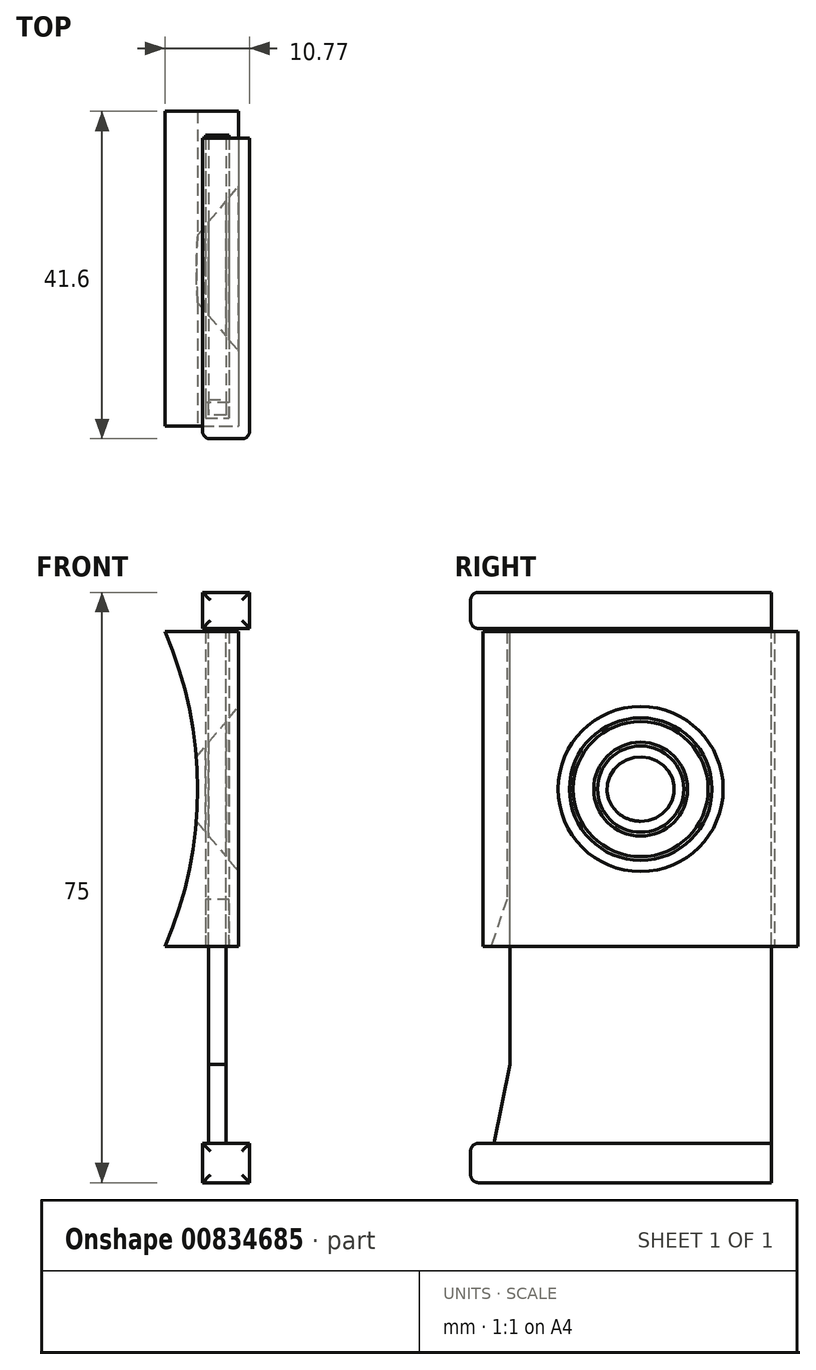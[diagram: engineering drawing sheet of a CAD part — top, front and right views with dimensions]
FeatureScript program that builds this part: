
annotation { "Feature Type Name" : "Feature", "Feature Type Description" : "" }
export const myFeature = defineFeature(function(context is Context, id is Id, definition is map)
    precondition{}
    {
        {
            var Q0;
            Q0=qCreatedBy(makeId("Top.planeOp"),FACE);
            var sketch = newSketch(context, id + "F0", { "sketchPlane" : qUnion([Q0])});
            skLineSegment(sketch, "E0.bottom", {"start": v(0, 20) * mm, "end": v(10, 20) * mm});
            skLineSegment(sketch, "E0.top", {"start": v(0, -20) * mm, "end": v(10, -20) * mm});
            skLineSegment(sketch, "E0.left", {"start": v(0, 20) * mm, "end": v(0, -20) * mm});
            skLineSegment(sketch, "E0.right", {"start": v(10, 20) * mm, "end": v(10, -20) * mm});
            skCircle(sketch, "E1", {"center": v(-41.2, 0) * mm, "radius": 50 * mm});
            skLineSegment(sketch, "E2.bottom", {"start": v(10, 20) * mm, "end": v(13, 20) * mm});
            skLineSegment(sketch, "E2.top", {"start": v(10, 17) * mm, "end": v(13, 17) * mm});
            skLineSegment(sketch, "E2.left", {"start": v(10, 20) * mm, "end": v(10, 17) * mm});
            skLineSegment(sketch, "E2.right", {"start": v(13, 20) * mm, "end": v(13, 17) * mm});
            skLineSegment(sketch, "E3.bottom", {"start": v(10, -20) * mm, "end": v(13, -20) * mm});
            skLineSegment(sketch, "E3.top", {"start": v(10, -17) * mm, "end": v(13, -17) * mm});
            skLineSegment(sketch, "E3.left", {"start": v(10, -20) * mm, "end": v(10, -17) * mm});
            skLineSegment(sketch, "E3.right", {"start": v(13, -20) * mm, "end": v(13, -17) * mm});
            skLineSegment(sketch, "E4.bottom", {"start": v(13, 20) * mm, "end": v(14.2, 20) * mm});
            skLineSegment(sketch, "E4.top", {"start": v(13, -20) * mm, "end": v(14.2, -20) * mm});
            skLineSegment(sketch, "E4.left", {"start": v(13, 20) * mm, "end": v(13, -20) * mm});
            skLineSegment(sketch, "E4.right", {"start": v(14.2, 20) * mm, "end": v(14.2, -20) * mm});
            skLineSegment(sketch, "E5.left", {"start": v(13, -20) * mm, "end": v(13, -20) * mm});
            skLineSegment(sketch, "E5.right", {"start": v(14.2, -20) * mm, "end": v(14.2, -20) * mm});
            skSolve(sketch);
        }
        {
            var Q0;
            Q0=makeQuery(id+"F0.imprint","IMPRINT",FACE,{"disambiguationData":[TD([[makeQuery(id+"F0.imprint","IMPRINT",EDGE,{"derivedFrom":sQuery(id+"F0.wireOp",EDGE,"E0.right")}),-1.0]])]});
            var Q1;
            {var subQ0=sQuery(id+"F0.wireOp",EDGE,"E2.bottom");Q1=makeQuery(id+"F0.imprint","IMPRINT",FACE,{"disambiguationData":[TD([[makeQuery(id+"F0.imprint","IMPRINT",EDGE,{"derivedFrom":subQ0}),-1.0]])]});}
            var Q2;
            {var subQ4=sQuery(id+"F0.wireOp",EDGE,"E4.bottom");Q2=makeQuery(id+"F0.imprint","IMPRINT",FACE,{"disambiguationData":[TD([[makeQuery(id+"F0.imprint","IMPRINT",EDGE,{"derivedFrom":subQ4}),-1.0]])]});}
            var Q3;
            {var subQ0=sQuery(id+"F0.wireOp",EDGE,"E3.bottom");Q3=makeQuery(id+"F0.imprint","IMPRINT",FACE,{"disambiguationData":[TD([[makeQuery(id+"F0.imprint","IMPRINT",EDGE,{"derivedFrom":subQ0}),1.0]])]});}
            var Q4;
            {var subQ0=sQuery(id+"F0.wireOp",EDGE,"E0.left");Q4=makeQuery(id+"F0.imprint","IMPRINT",FACE,{"disambiguationData":[TD([[makeQuery(id+"F0.imprint","IMPRINT",EDGE,{"derivedFrom":subQ0}),1.0]])]});}
            extrude(context, id + "F1", {"entities" : qUnion([Q0, Q1, Q2, Q3, Q4]), "endBound" : BoundingType.SYMMETRIC, "depth" : 40 * mm, "offsetDistance" : 25 * mm});
        }
        {
            var Q0;
            Q0=qCreatedBy(makeId("Front.planeOp"),FACE);
            var sketch = newSketch(context, id + "F2", { "sketchPlane" : qUnion([Q0])});
            skCircle(sketch, "E6", {"center": v(-41, 0) * mm, "radius": 50 * mm});
            skSolve(sketch);
        }
        {
            var Q0;
            Q0=qSketchRegion(id+"F2",true);
            extrude(context, id + "F3", {"entities" : qUnion([Q0]), "operationType" : NewBodyOperationType.REMOVE, "endBound" : BoundingType.SYMMETRIC, "oppositeDirection" : true, "depth" : 50 * mm, "offsetDistance" : 25 * mm});
        }
        {
            var Q0;
            Q0=makeQuery(id+"F1.opExtrude","CAP_FACE",FACE,{"disambiguationData":[OSD([sQuery(id+"F0.wireOp",EDGE,"E0.bottom"),sQuery(id+"F0.wireOp",EDGE,"E0.top"),sQuery(id+"F0.wireOp",EDGE,"E0.left"),sQuery(id+"F0.wireOp",EDGE,"E0.right"),sQuery(id+"F0.wireOp",EDGE,"E2.bottom"),sQuery(id+"F0.wireOp",EDGE,"E2.top"),sQuery(id+"F0.wireOp",EDGE,"E3.bottom"),sQuery(id+"F0.wireOp",EDGE,"E3.top"),sQuery(id+"F0.wireOp",EDGE,"E4.bottom"),sQuery(id+"F0.wireOp",EDGE,"E4.left"),sQuery(id+"F0.wireOp",EDGE,"E4.right"),sQuery(id+"F0.wireOp",EDGE,"E4.top")])],"isStart":false});
            var sketch = newSketch(context, id + "F4", { "sketchPlane" : qUnion([Q0])});
            skLineSegment(sketch, "E7.bottom", {"start": v(10.4, 16.6) * mm, "end": v(12.6, 16.6) * mm});
            skLineSegment(sketch, "E7.top", {"start": v(10.4, -16.6) * mm, "end": v(12.6, -16.6) * mm});
            skLineSegment(sketch, "E7.left", {"start": v(10.4, 16.6) * mm, "end": v(10.4, -16.6) * mm});
            skLineSegment(sketch, "E7.right", {"start": v(12.6, 16.6) * mm, "end": v(12.6, -16.6) * mm});
            skSolve(sketch);
        }
        {
            var Q0;
            Q0=makeQuery(id+"F4.imprint","IMPRINT",FACE,{"disambiguationData":[TD([[makeQuery(id+"F4.imprint","IMPRINT",EDGE,{"derivedFrom":sQuery(id+"F4.wireOp",EDGE,"E7.bottom")}),-1.0]])]});
            extrude(context, id + "F5", {"entities" : qUnion([Q0]), "oppositeDirection" : true, "depth" : 70 * mm, "offsetDistance" : 25 * mm, "hasSecondDirection" : true, "secondDirectionOppositeDirection" : false, "secondDirectionDepth" : 5 * mm});
        }
        {
            var Q0;
            Q0=qCreatedBy(makeId("Right.planeOp"),FACE);
            cPlane(context, id + "F6", {"entities" : qUnion([Q0]), "cplaneType" : CPlaneType.OFFSET, "offset" : 7.92 * mm, "width" : 150 * mm, "height" : 150 * mm});
        }
        {
            var Q0;
            Q0=qCreatedBy(id+"F6.planeOp",FACE);
            var sketch = newSketch(context, id + "F7", { "sketchPlane" : qUnion([Q0])});
            skCircle(sketch, "E8", {"center": v(0, 0) * mm, "radius": 3 * mm});
            skSolve(sketch);
        }
        {
            var Q0;
            Q0=qSketchRegion(id+"F7",true);
            extrude(context, id + "F8", {"entities" : qUnion([Q0]), "operationType" : NewBodyOperationType.REMOVE, "depth" : 25 * mm, "offsetDistance" : 25 * mm, "hasDraft" : true, "draftAngle" : 50 * degree});
        }
        {
            var Q0;
            Q0=makeQuery(id+"F5.opExtrude","SWEPT_FACE",FACE,{"disambiguationData":[OSD([sQuery(id+"F4.wireOp",EDGE,"E7.right")])]});
            var sketch = newSketch(context, id + "F9", { "sketchPlane" : qUnion([Q0])});
            skLineSegment(sketch, "E9.bottom", {"start": v(16.6, 25) * mm, "end": v(-21.6, 25) * mm});
            skLineSegment(sketch, "E9.top", {"start": v(16.6, 20.4) * mm, "end": v(-21.6, 20.4) * mm});
            skLineSegment(sketch, "E9.left", {"start": v(16.6, 25) * mm, "end": v(16.6, 20.4) * mm});
            skLineSegment(sketch, "E9.right", {"start": v(-21.6, 25) * mm, "end": v(-21.6, 20.4) * mm});
            skLineSegment(sketch, "E10.bottom", {"start": v(16.6, -50) * mm, "end": v(-21.6, -50) * mm});
            skLineSegment(sketch, "E10.top", {"start": v(16.6, -45) * mm, "end": v(-21.6, -45) * mm});
            skLineSegment(sketch, "E10.left", {"start": v(16.6, -50) * mm, "end": v(16.6, -45) * mm});
            skLineSegment(sketch, "E10.right", {"start": v(-21.6, -50) * mm, "end": v(-21.6, -45) * mm});
            skSolve(sketch);
        }
        {
            var Q0;
            Q0=qSketchRegion(id+"F9",true);
            extrude(context, id + "F10", {"entities" : qUnion([Q0]), "operationType" : NewBodyOperationType.ADD, "depth" : 3 * mm, "offsetDistance" : 25 * mm, "hasSecondDirection" : true, "secondDirectionOppositeDirection" : true, "secondDirectionDepth" : 3 * mm});
        }
        {
            var Q0;
            Q0=makeQuery(id+"F10.opExtrude","SWEPT_FACE",FACE,{"disambiguationData":[OSD([sQuery(id+"F9.wireOp",EDGE,"E10.right")])]});
            var Q1;
            Q1=makeQuery(id+"F10.opExtrude","SWEPT_FACE",FACE,{"disambiguationData":[OSD([sQuery(id+"F9.wireOp",EDGE,"E9.right")])]});
            fillet(context, id + "F11", {"entities" : qUnion([Q0, Q1]), "radius" : 1 * mm, "tangentPropagation" : true, "allowEdgeOverflow" : false});
        }
        {
            var Q0;
            Q0=makeQuery(id+"F10.boolean.opBoolean","INTERSECT",EDGE,{"derivedFrom":[makeQuery(id+"F5.opExtrude","SWEPT_FACE",FACE,{"disambiguationData":[OSD([sQuery(id+"F4.wireOp",EDGE,"E7.top")])]}),makeQuery(id+"F10.opExtrude","SWEPT_FACE",FACE,{"disambiguationData":[OSD([sQuery(id+"F9.wireOp",EDGE,"E10.top")])]})]});
            chamfer(context, id + "F12", {"entities" : qUnion([Q0]), "chamferType" : ChamferType.TWO_OFFSETS, "width1" : 10 * mm, "oppositeDirection" : false, "width2" : 2 * mm, "tangentPropagation" : true});
        }
        {
            var Q0;
            Q0=makeQuery(id+"F1.opExtrude","CAP_EDGE",EDGE,{"disambiguationData":[OSD([sQuery(id+"F0.wireOp",EDGE,"E3.top")])],"isStart":true});
            chamfer(context, id + "F13", {"entities" : qUnion([Q0]), "chamferType" : ChamferType.TWO_OFFSETS, "width1" : 2 * mm, "oppositeDirection" : false, "width2" : 6 * mm, "tangentPropagation" : true});
        }
    });
